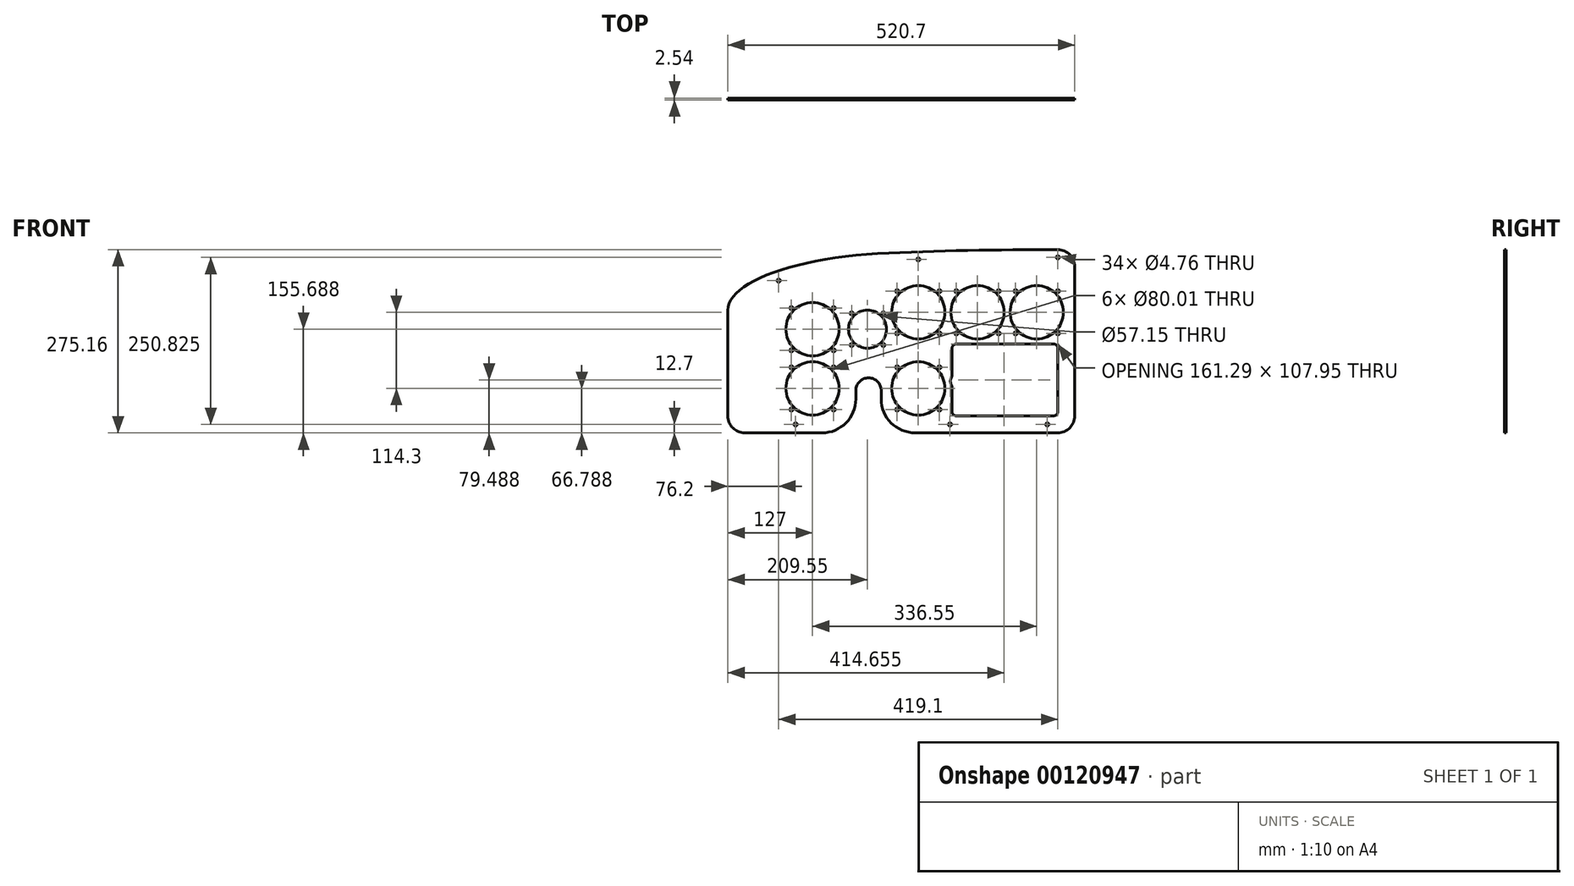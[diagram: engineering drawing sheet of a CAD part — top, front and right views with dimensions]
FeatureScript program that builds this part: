
annotation { "Feature Type Name" : "Feature", "Feature Type Description" : "" }
export const myFeature = defineFeature(function(context is Context, id is Id, definition is map)
    precondition{}
    {
        {
            var Q0;
            Q0=qCreatedBy(makeId("Front.planeOp"),FACE);
            var sketch = newSketch(context, id + "F0", { "sketchPlane" : qUnion([Q0])});
            skCircle(sketch, "E0", {"center": v(-180.98, -261.95) * mm, "radius": 2.38 * mm});
            skLineSegment(sketch, "E1", {"start": v(-514.35, -90.5) * mm, "end": v(-228.58, -90.5) * mm, "construction": true});
            skLineSegment(sketch, "E2", {"start": v(-228.58, -3.02) * mm, "end": v(-228.58, -90.5) * mm, "construction": true});
            skPoint(sketch, "E3.visualSharp", {"position": v(-508.1, -268.2) * mm});
            skPoint(sketch, "E4.visualSharp", {"position": v(-0.1, -268.3) * mm});
            skPoint(sketch, "E5.visualSharp", {"position": v(0, 0) * mm});
            skCircle(sketch, "E6", {"center": v(-34.93, -261.95) * mm, "radius": 2.38 * mm});
            skCircle(sketch, "E7", {"center": v(-412.75, -261.95) * mm, "radius": 2.38 * mm});
            skCircle(sketch, "E8", {"center": v(-19.05, -11.13) * mm, "radius": 2.38 * mm});
            skCircle(sketch, "E9", {"center": v(-228.6, -14.19) * mm, "radius": 2.38 * mm});
            skCircle(sketch, "E10", {"center": v(-438.15, -46.05) * mm, "radius": 2.38 * mm});
            skLineSegment(sketch, "E11", {"start": v(-322.28, -211.04) * mm, "end": v(-284.18, -211.04) * mm, "construction": true});
            skPoint(sketch, "E12.visualSharp", {"position": v(-277.83, -268.19) * mm});
            skPoint(sketch, "E13.visualSharp", {"position": v(-315.93, -268.19) * mm});
            skLineSegment(sketch, "E14.bottom", {"start": v(-171.45, -141.19) * mm, "end": v(-25.4, -141.19) * mm});
            skLineSegment(sketch, "E14.top", {"start": v(-171.45, -249.14) * mm, "end": v(-25.4, -249.14) * mm});
            skLineSegment(sketch, "E14.left", {"start": v(-177.8, -147.54) * mm, "end": v(-177.8, -189.96) * mm});
            skLineSegment(sketch, "E14.right", {"start": v(-19.05, -147.54) * mm, "end": v(-19.05, -242.79) * mm});
            skPoint(sketch, "E15.visualSharp", {"position": v(-177.8, -141.19) * mm});
            skArc(sketch, "E15.filletArc", {"start": v(-171.45, -141.19) * mm, "mid": v(-175.94, -143.05) * mm, "end": v(-177.8, -147.54) * mm});
            skPoint(sketch, "E16.visualSharp", {"position": v(-19.05, -141.19) * mm});
            skArc(sketch, "E16.filletArc", {"start": v(-19.05, -147.54) * mm, "mid": v(-20.9, -143.05) * mm, "end": v(-25.4, -141.19) * mm});
            skPoint(sketch, "E17.visualSharp", {"position": v(-19.05, -249.14) * mm});
            skArc(sketch, "E17.filletArc", {"start": v(-25.4, -249.14) * mm, "mid": v(-20.9, -247.28) * mm, "end": v(-19.05, -242.79) * mm});
            skPoint(sketch, "E18.visualSharp", {"position": v(-177.8, -249.14) * mm});
            skArc(sketch, "E18.filletArc", {"start": v(-177.8, -242.79) * mm, "mid": v(-175.94, -247.28) * mm, "end": v(-171.45, -249.14) * mm});
            skArc(sketch, "E19", {"start": v(-19.01, 0.5) * mm, "mid": v(-154.45, -0.8) * mm, "end": v(-289.82, -5.14) * mm});
            skEllipticalArc(sketch, "E20.trimOffspring", {});
            skLineSegment(sketch, "E21.0", {"start": v(-514.35, -249.25) * mm, "end": v(-514.35, -90.5) * mm});
            skLineSegment(sketch, "E22.0", {"start": v(-373.08, -274.65) * mm, "end": v(-488.95, -274.65) * mm});
            skLineSegment(sketch, "E23.0", {"start": v(-19.05, -274.54) * mm, "end": v(-233.38, -274.54) * mm});
            skLineSegment(sketch, "E24.0", {"start": v(6.35, -24.9) * mm, "end": v(6.35, -249.14) * mm});
            skArc(sketch, "E25.filletArc", {"start": v(-19.05, -274.54) * mm, "mid": v(-1.09, -267.1) * mm, "end": v(6.35, -249.14) * mm});
            skArc(sketch, "E26.filletArc", {"start": v(-514.35, -249.25) * mm, "mid": v(-506.91, -267.21) * mm, "end": v(-488.95, -274.65) * mm});
            skArc(sketch, "E27.filletArc", {"start": v(6.35, -24.9) * mm, "mid": v(-1.08, -6.95) * mm, "end": v(-19.01, 0.5) * mm});
            skArc(sketch, "E28", {"start": v(-177.8, -189.96) * mm, "mid": v(-180.34, -196.94) * mm, "end": v(-177.8, -203.92) * mm});
            skLineSegment(sketch, "E29", {"start": v(-180.34, -28.59) * mm, "end": v(-180.34, -211.7) * mm, "construction": true});
            skLineSegment(sketch, "E30.trimOffspring", {"start": v(-177.8, -203.92) * mm, "end": v(-177.8, -242.79) * mm});
            skLineSegment(sketch, "E31.0", {"start": v(-322.28, -211.04) * mm, "end": v(-322.28, -223.85) * mm});
            skLineSegment(sketch, "E32.0", {"start": v(-284.18, -211.04) * mm, "end": v(-284.18, -223.74) * mm});
            skArc(sketch, "E33", {"start": v(-284.18, -211.04) * mm, "mid": v(-303.23, -191.99) * mm, "end": v(-322.28, -211.04) * mm});
            skArc(sketch, "E34.filletArc", {"start": v(-373.08, -274.65) * mm, "mid": v(-337.15, -259.77) * mm, "end": v(-322.28, -223.85) * mm});
            skArc(sketch, "E35.filletArc", {"start": v(-284.18, -223.74) * mm, "mid": v(-269.3, -259.66) * mm, "end": v(-233.38, -274.54) * mm});
            const initialGuessF0  = {"E20.trimOffspring": [-0.22858269617228638, -0.09038691560837803, -1, 0, 0.28576754158477813, 0.0872793365103509, 4.928366700610943, 0.0012979523901006547]};
            skSetInitialGuess(sketch, initialGuessF0);
            skSolve(sketch);
        }
        {
            var Q0;
            Q0 = qSketchRegion(id + "F0", true);
            extrude(context, id + "F1", {"entities" : qUnion([Q0]), "depth" : 2.54 * mm});
        }
        {
            var Q0;
            Q0=makeQuery(id+"F1.opExtrude","CAP_FACE",FACE,{"disambiguationData":[OSD([sQuery(id+"F0.wireOp",EDGE,"E0"),sQuery(id+"F0.wireOp",EDGE,"E6"),sQuery(id+"F0.wireOp",EDGE,"E7"),sQuery(id+"F0.wireOp",EDGE,"E8"),sQuery(id+"F0.wireOp",EDGE,"E9"),sQuery(id+"F0.wireOp",EDGE,"E10"),sQuery(id+"F0.wireOp",EDGE,"WbkpdAwD-11kY-b4Ex-kZiu-tVNXVgqoXC4c"),sQuery(id+"F0.wireOp",EDGE,"qMZugXpT-DE4o-xRzg-C20Y-DulmbLEhYvK7"),sQuery(id+"F0.wireOp",EDGE,"aUUCGkwf-wXAW-N3Ib-32mK-aVH7npSlMp4z"),sQuery(id+"F0.wireOp",EDGE,"E14.bottom"),sQuery(id+"F0.wireOp",EDGE,"E14.top"),sQuery(id+"F0.wireOp",EDGE,"E14.left"),sQuery(id+"F0.wireOp",EDGE,"E14.right"),sQuery(id+"F0.wireOp",EDGE,"E15.filletArc"),sQuery(id+"F0.wireOp",EDGE,"E16.filletArc"),sQuery(id+"F0.wireOp",EDGE,"E17.filletArc"),sQuery(id+"F0.wireOp",EDGE,"E18.filletArc"),sQuery(id+"F0.wireOp",EDGE,"E19"),sQuery(id+"F0.wireOp",EDGE,"E20.trimOffspring"),sQuery(id+"F0.wireOp",EDGE,"E21.0"),sQuery(id+"F0.wireOp",EDGE,"E22.0"),sQuery(id+"F0.wireOp",EDGE,"E23.0"),sQuery(id+"F0.wireOp",EDGE,"E24.0"),sQuery(id+"F0.wireOp",EDGE,"E25.filletArc"),sQuery(id+"F0.wireOp",EDGE,"E26.filletArc"),sQuery(id+"F0.wireOp",EDGE,"f7f968a2-535c-475c-8e79-3eded501f02a.filletArc"),sQuery(id+"F0.wireOp",EDGE,"4cb937f4-15b8-436b-a888-d3fb9ea72733.filletArc"),sQuery(id+"F0.wireOp",EDGE,"E27.filletArc"),sQuery(id+"F0.wireOp",EDGE,"E28"),sQuery(id+"F0.wireOp",EDGE,"E30.trimOffspring")])],"isStart":false});
            var sketch = newSketch(context, id + "F2", { "sketchPlane" : qUnion([Q0])});
            skCircle(sketch, "E36", {"center": v(-50.8, -93.56) * mm, "radius": 40 * mm});
            skCircle(sketch, "E37.1.0.0", {"center": v(-139.7, -93.56) * mm, "radius": 40 * mm});
            skLineSegment(sketch, "E37.direction1", {"start": v(-50.8, -93.56) * mm, "end": v(-139.7, -93.56) * mm, "construction": true});
            skLineSegment(sketch, "E37.direction2", {"start": v(-50.8, -93.56) * mm, "end": v(-50.8, -188.81) * mm, "construction": true});
            skCircle(sketch, "E38.0.2.0", {"center": v(-228.6, -93.56) * mm, "radius": 40 * mm});
            skCircle(sketch, "E39", {"center": v(-304.8, -118.96) * mm, "radius": 28.58 * mm});
            skLineSegment(sketch, "E40", {"start": v(51.13, -268.19) * mm, "end": v(-558.71, -268.19) * mm, "construction": true});
            skCircle(sketch, "E41", {"center": v(-19.05, -125.31) * mm, "radius": 2.38 * mm});
            skCircle(sketch, "E42.1.0", {"center": v(-82.55, -125.31) * mm, "radius": 2.38 * mm});
            skCircle(sketch, "E42.2.0", {"center": v(-82.55, -61.81) * mm, "radius": 2.38 * mm});
            skCircle(sketch, "E42.3.0", {"center": v(-19.05, -61.81) * mm, "radius": 2.38 * mm});
            skLineSegment(sketch, "E42.anchor1", {"start": v(-50.8, -93.56) * mm, "end": v(-19.05, -125.31) * mm, "construction": true});
            skLineSegment(sketch, "E42.anchor2", {"start": v(-50.8, -93.56) * mm, "end": v(-19.05, -61.81) * mm, "construction": true});
            skLineSegment(sketch, "E43.direction1", {"start": v(-82.55, -61.81) * mm, "end": v(-177.8, -61.81) * mm, "construction": true});
            skLineSegment(sketch, "E43.direction2", {"start": v(-82.55, -61.81) * mm, "end": v(-82.55, -157.06) * mm, "construction": true});
            skCircle(sketch, "E44", {"center": v(-280.97, -142.79) * mm, "radius": 2.38 * mm});
            skCircle(sketch, "E45.1.0", {"center": v(-280.97, -95.14) * mm, "radius": 2.38 * mm});
            skCircle(sketch, "E45.2.0", {"center": v(-328.63, -95.14) * mm, "radius": 2.38 * mm});
            skCircle(sketch, "E45.3.0", {"center": v(-328.63, -142.79) * mm, "radius": 2.38 * mm});
            skCircle(sketch, "E46.0.1.4", {"center": v(-228.6, -207.86) * mm, "radius": 40 * mm});
            skCircle(sketch, "E46.1.0.4", {"center": v(-387.35, -118.96) * mm, "radius": 40 * mm});
            skCircle(sketch, "E46.1.1.4", {"center": v(-387.35, -207.86) * mm, "radius": 40 * mm});
            skCircle(sketch, "E47.1.0.0", {"center": v(-171.45, -125.31) * mm, "radius": 2.38 * mm});
            skCircle(sketch, "E47.1.0.1", {"center": v(-107.95, -125.31) * mm, "radius": 2.38 * mm});
            skCircle(sketch, "E47.1.0.2", {"center": v(-107.95, -61.81) * mm, "radius": 2.38 * mm});
            skCircle(sketch, "E47.1.0.3", {"center": v(-171.45, -61.81) * mm, "radius": 2.38 * mm});
            skCircle(sketch, "E47.2.0.0", {"center": v(-260.35, -125.31) * mm, "radius": 2.38 * mm});
            skCircle(sketch, "E47.2.0.1", {"center": v(-196.85, -125.31) * mm, "radius": 2.38 * mm});
            skCircle(sketch, "E47.2.0.2", {"center": v(-196.85, -61.81) * mm, "radius": 2.38 * mm});
            skCircle(sketch, "E47.2.0.3", {"center": v(-260.35, -61.81) * mm, "radius": 2.38 * mm});
            skLineSegment(sketch, "E47.direction1", {"start": v(-82.55, -125.31) * mm, "end": v(-171.45, -125.31) * mm, "construction": true});
            skCircle(sketch, "E48.0.1.0", {"center": v(-260.35, -176.11) * mm, "radius": 2.38 * mm});
            skCircle(sketch, "E48.0.1.1", {"center": v(-260.35, -239.61) * mm, "radius": 2.38 * mm});
            skCircle(sketch, "E48.0.1.2", {"center": v(-196.85, -176.11) * mm, "radius": 2.38 * mm});
            skCircle(sketch, "E48.0.1.3", {"center": v(-196.85, -239.61) * mm, "radius": 2.38 * mm});
            skLineSegment(sketch, "E48.direction1", {"start": v(-260.35, -125.31) * mm, "end": v(-232.66, -140.72) * mm, "construction": true});
            skLineSegment(sketch, "E48.direction2", {"start": v(-260.35, -125.31) * mm, "end": v(-260.35, -239.61) * mm, "construction": true});
            skLineSegment(sketch, "E49.direction1", {"start": v(-260.35, -239.61) * mm, "end": v(-419.1, -239.61) * mm, "construction": true});
            skCircle(sketch, "E50.0.1.0", {"center": v(-419.1, -176.11) * mm, "radius": 2.38 * mm});
            skCircle(sketch, "E50.2.1.0", {"center": v(-355.6, -176.11) * mm, "radius": 2.38 * mm});
            skCircle(sketch, "E50.4.1.0", {"center": v(-355.6, -239.61) * mm, "radius": 2.38 * mm});
            skCircle(sketch, "E50.6.1.0", {"center": v(-419.1, -239.61) * mm, "radius": 2.38 * mm});
            skCircle(sketch, "E51.0.1.0", {"center": v(-355.6, -150.71) * mm, "radius": 2.38 * mm});
            skCircle(sketch, "E51.0.1.1", {"center": v(-419.1, -87.21) * mm, "radius": 2.38 * mm});
            skCircle(sketch, "E51.0.1.2", {"center": v(-355.6, -87.21) * mm, "radius": 2.38 * mm});
            skCircle(sketch, "E51.0.1.3", {"center": v(-419.1, -150.71) * mm, "radius": 2.38 * mm});
            skLineSegment(sketch, "E51.direction1", {"start": v(-419.1, -239.61) * mm, "end": v(-393.7, -239.61) * mm, "construction": true});
            skLineSegment(sketch, "E51.direction2", {"start": v(-419.1, -239.61) * mm, "end": v(-419.1, -150.71) * mm, "construction": true});
            skSolve(sketch);
        }
        {
            var Q0;
            Q0 = qSketchRegion(id + "F2", true);
            extrude(context, id + "F3", {"entities" : qUnion([Q0]), "operationType" : NewBodyOperationType.REMOVE, "endBound" : BoundingType.THROUGH_ALL, "oppositeDirection" : true, "depth" : 25.4 * mm});
        }
    });
